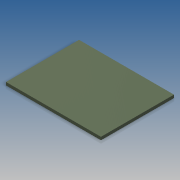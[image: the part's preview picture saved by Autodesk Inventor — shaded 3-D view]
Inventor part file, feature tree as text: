
AUTODESK INVENTOR PART (.ipt)
format: ipt  version: 2016 SP2 (Build 200236200, 236)  size: 86,016 bytes
history: native  units: in
note: dims shown in document units (in); Inventor stores cm internally (conversion verified against a paired STEP export)
features: extrude x1, sketch x1
ambient origin geometry x8: Origin, YZ Plane, XZ Plane, XY Plane, X Axis, Y Axis, Z Axis, Center Point
bodies: Solid1 (feature_tree)
feature tree (2):
  extrude  "Extrusion1"  Depth=2.0472in
  sketch  "Sketch2"  dims[d0=1.5748in d1=2.0472in d2=0.063in d3=0.0in]
